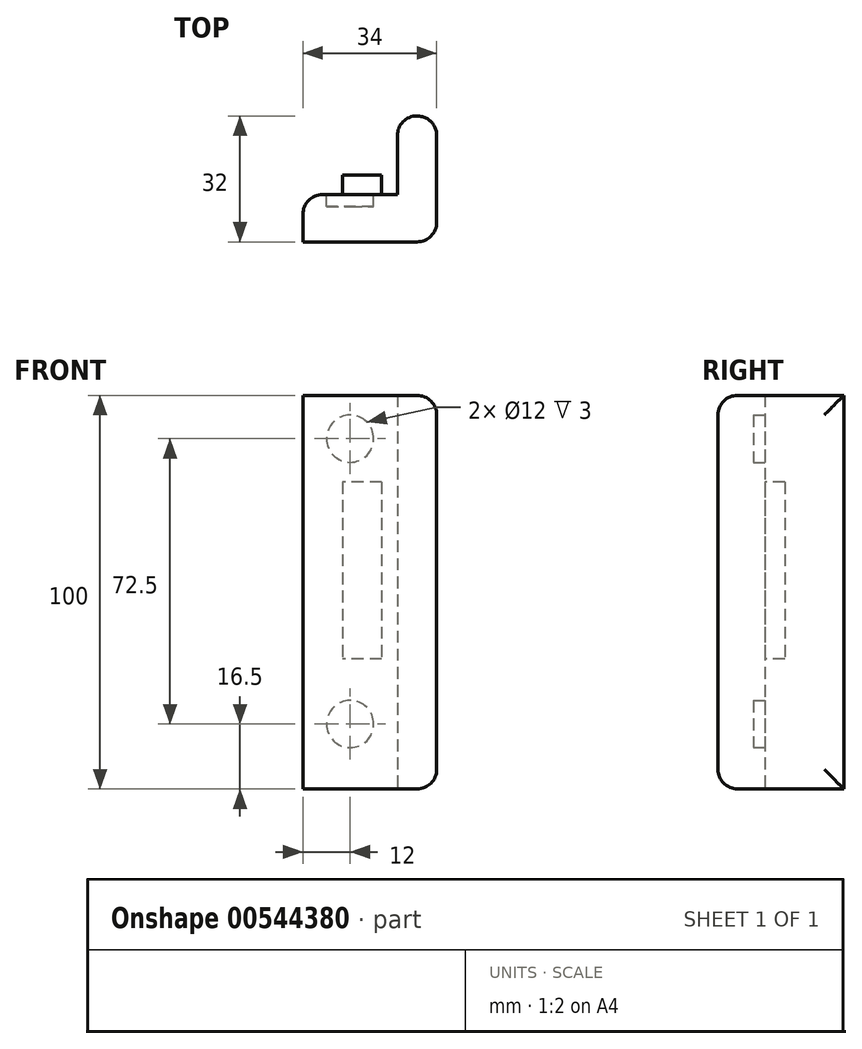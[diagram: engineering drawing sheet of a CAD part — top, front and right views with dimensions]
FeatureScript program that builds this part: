
annotation { "Feature Type Name" : "Feature", "Feature Type Description" : "" }
export const myFeature = defineFeature(function(context is Context, id is Id, definition is map)
    precondition{}
    {
        {
            var Q0;
            Q0=qCreatedBy(makeId("Top.planeOp"),FACE);
            var sketch = newSketch(context, id + "F0", { "sketchPlane" : qUnion([Q0])});
            skLineSegment(sketch, "E0", {"start": v(0, 0) * mm, "end": v(0, 20) * mm});
            skLineSegment(sketch, "E1", {"start": v(0, 20) * mm, "end": v(-10, 20) * mm});
            skLineSegment(sketch, "E2", {"start": v(-10, 20) * mm, "end": v(-10, 0) * mm});
            skLineSegment(sketch, "E3", {"start": v(-10, 0) * mm, "end": v(-34, 0) * mm});
            skLineSegment(sketch, "E4", {"start": v(-34, 0) * mm, "end": v(-34, -12) * mm});
            skLineSegment(sketch, "E5", {"start": v(-34, -12) * mm, "end": v(0, -12) * mm});
            skLineSegment(sketch, "E6", {"start": v(0, -12) * mm, "end": v(0, 0) * mm});
            skSolve(sketch);
        }
        {
            var Q0;
            Q0=makeQuery(id+"F0.imprint","IMPRINT",FACE,{"disambiguationData":[TD([[makeQuery(id+"F0.imprint","IMPRINT",EDGE,{"derivedFrom":sQuery(id+"F0.wireOp",EDGE,"E0")}),1.0]])]});
            extrude(context, id + "F1", {"entities" : qUnion([Q0]), "depth" : 50 * mm, "offsetDistance" : 25 * mm, "hasSecondDirection" : true, "secondDirectionOppositeDirection" : true, "secondDirectionDepth" : 50 * mm});
        }
        {
            var Q0;
            Q0=makeQuery(id+"F1.opExtrude","SWEPT_FACE",FACE,{"disambiguationData":[OSD([sQuery(id+"F0.wireOp",EDGE,"E3")])]});
            var sketch = newSketch(context, id + "F2", { "sketchPlane" : qUnion([Q0])});
            skLineSegment(sketch, "E7.bottom", {"start": v(14, 28) * mm, "end": v(24, 28) * mm});
            skLineSegment(sketch, "E7.top", {"start": v(14, -17) * mm, "end": v(24, -17) * mm});
            skLineSegment(sketch, "E7.left", {"start": v(14, 28) * mm, "end": v(14, -17) * mm});
            skLineSegment(sketch, "E7.right", {"start": v(24, 28) * mm, "end": v(24, -17) * mm});
            skSolve(sketch);
        }
        {
            var Q0;
            Q0=makeQuery(id+"F2.imprint","IMPRINT",FACE,{"disambiguationData":[TD([[makeQuery(id+"F2.imprint","IMPRINT",EDGE,{"derivedFrom":sQuery(id+"F2.wireOp",EDGE,"E7.bottom")}),-1.0]])]});
            extrude(context, id + "F3", {"entities" : qUnion([Q0]), "operationType" : NewBodyOperationType.ADD, "depth" : 5 * mm, "offsetDistance" : 25 * mm});
        }
        {
            var Q0;
            Q0=makeQuery(id+"F1.opExtrude","SWEPT_FACE",FACE,{"disambiguationData":[OSD([sQuery(id+"F0.wireOp",EDGE,"E3")])]});
            var sketch = newSketch(context, id + "F4", { "sketchPlane" : qUnion([Q0])});
            skCircle(sketch, "E8", {"center": v(22, 39) * mm, "radius": 6 * mm});
            skCircle(sketch, "E9", {"center": v(22, -33.5) * mm, "radius": 6 * mm});
            skLineSegment(sketch, "E10", {"start": v(22, -50) * mm, "end": v(22, 50) * mm, "construction": true});
            skSolve(sketch);
        }
        {
            var Q0;
            Q0=makeQuery(id+"F4.imprint","IMPRINT",FACE,{"disambiguationData":[TD([[makeQuery(id+"F4.imprint","IMPRINT",EDGE,{"derivedFrom":sQuery(id+"F4.wireOp",EDGE,"E8")}),1.0]])]});
            var Q1;
            Q1=makeQuery(id+"F4.imprint","IMPRINT",FACE,{"disambiguationData":[TD([[makeQuery(id+"F4.imprint","IMPRINT",EDGE,{"derivedFrom":sQuery(id+"F4.wireOp",EDGE,"E9")}),1.0]])]});
            extrude(context, id + "F5", {"entities" : qUnion([Q0, Q1]), "operationType" : NewBodyOperationType.REMOVE, "oppositeDirection" : true, "depth" : 3 * mm, "offsetDistance" : 25 * mm});
        }
        {
            var Q0;
            Q0=makeQuery(id+"F1.opExtrude","SWEPT_EDGE",EDGE,{"disambiguationData":[OSD([sQuery(id+"F0.wireOp",EDGE,"E5"),sQuery(id+"F0.wireOp",EDGE,"E6")])]});
            var Q1;
            Q1=makeQuery(id+"F1.opExtrude","CAP_EDGE",EDGE,{"disambiguationData":[OSD([sQuery(id+"F0.wireOp",EDGE,"E0"),sQuery(id+"F0.wireOp",EDGE,"E6")])],"isStart":false});
            var Q2;
            Q2=makeQuery(id+"F1.opExtrude","CAP_EDGE",EDGE,{"disambiguationData":[OSD([sQuery(id+"F0.wireOp",EDGE,"E5")])],"isStart":false});
            var Q3;
            Q3=makeQuery(id+"F1.opExtrude","CAP_EDGE",EDGE,{"disambiguationData":[OSD([sQuery(id+"F0.wireOp",EDGE,"E5")])],"isStart":true});
            var Q4;
            Q4=makeQuery(id+"F1.opExtrude","CAP_EDGE",EDGE,{"disambiguationData":[OSD([sQuery(id+"F0.wireOp",EDGE,"E0"),sQuery(id+"F0.wireOp",EDGE,"E6")])],"isStart":true});
            var Q5;
            Q5=makeQuery(id+"F1.opExtrude","SWEPT_EDGE",EDGE,{"disambiguationData":[OSD([sQuery(id+"F0.wireOp",EDGE,"E1"),sQuery(id+"F0.wireOp",EDGE,"E2")])]});
            var Q6;
            Q6=makeQuery(id+"F1.opExtrude","SWEPT_EDGE",EDGE,{"disambiguationData":[OSD([sQuery(id+"F0.wireOp",EDGE,"E0"),sQuery(id+"F0.wireOp",EDGE,"E1")])]});
            var Q7;
            Q7=makeQuery(id+"F1.opExtrude","SWEPT_EDGE",EDGE,{"disambiguationData":[OSD([sQuery(id+"F0.wireOp",EDGE,"E3"),sQuery(id+"F0.wireOp",EDGE,"E4")])]});
            fillet(context, id + "F6", {"entities" : qUnion([Q0, Q1, Q2, Q3, Q4, Q5, Q6, Q7]), "radius" : 5 * mm, "tangentPropagation" : true, "allowEdgeOverflow" : false});
        }
    });
